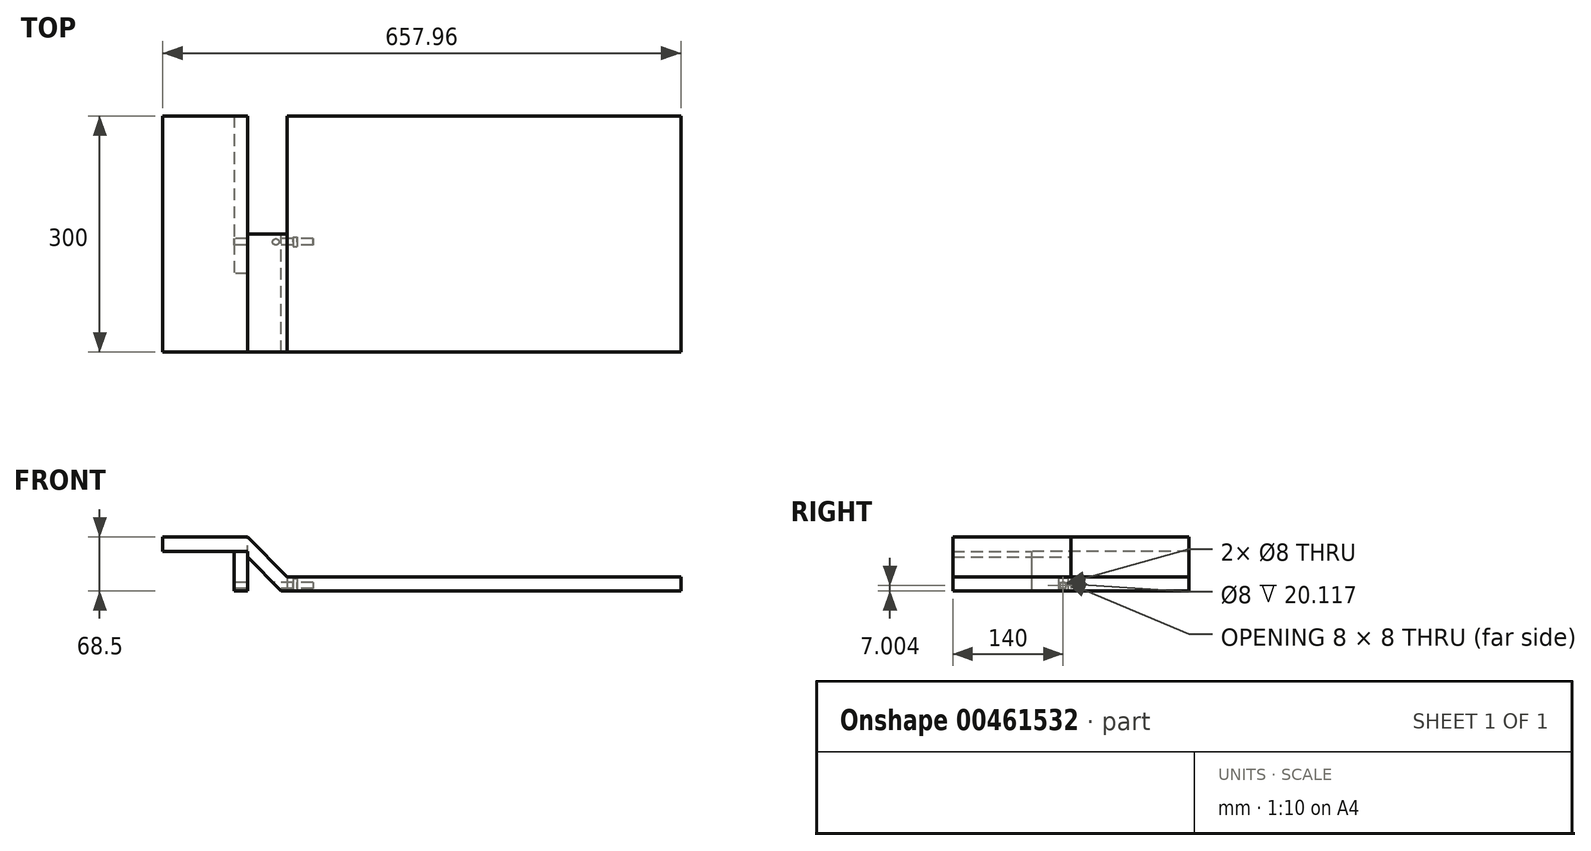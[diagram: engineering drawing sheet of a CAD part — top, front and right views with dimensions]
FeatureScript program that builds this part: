
annotation { "Feature Type Name" : "Feature", "Feature Type Description" : "" }
export const myFeature = defineFeature(function(context is Context, id is Id, definition is map)
    precondition{}
    {
        {
            var Q0;
            Q0=qCreatedBy(makeId("Front.planeOp"),FACE);
            var sketch = newSketch(context, id + "F0", { "sketchPlane" : qUnion([Q0])});
            skLineSegment(sketch, "E0.bottom", {"start": v(351.03, 31.5) * mm, "end": v(-148.97, 31.5) * mm});
            skLineSegment(sketch, "E0.top", {"start": v(351.03, 13.5) * mm, "end": v(-148.97, 13.5) * mm});
            skLineSegment(sketch, "E0.left", {"start": v(351.03, 31.5) * mm, "end": v(351.03, 13.5) * mm});
            skLineSegment(sketch, "E0.right", {"start": v(-148.97, 31.5) * mm, "end": v(-148.97, 13.5) * mm});
            skLineSegment(sketch, "E1.bottom", {"start": v(-148.97, 368.37) * mm, "end": v(-199.47, 368.37) * mm, "construction": true});
            skLineSegment(sketch, "E1.top", {"start": v(-148.97, -138.36) * mm, "end": v(-199.47, -138.36) * mm, "construction": true});
            skLineSegment(sketch, "E1.left", {"start": v(-148.97, 368.37) * mm, "end": v(-148.97, -138.36) * mm, "construction": true});
            skLineSegment(sketch, "E1.right", {"start": v(-199.47, 368.37) * mm, "end": v(-199.47, -138.36) * mm, "construction": true});
            skLineSegment(sketch, "E2", {"start": v(-148.97, 31.5) * mm, "end": v(-199.47, 82) * mm});
            skLineSegment(sketch, "E3", {"start": v(-148.97, 13.5) * mm, "end": v(-156.43, 13.5) * mm});
            skLineSegment(sketch, "E4", {"start": v(-156.43, 13.5) * mm, "end": v(-199.47, 56.54) * mm});
            skLineSegment(sketch, "E5", {"start": v(-199.47, 82) * mm, "end": v(-306.93, 82) * mm});
            skLineSegment(sketch, "E6", {"start": v(-199.47, 56.54) * mm, "end": v(-206.93, 64) * mm});
            skLineSegment(sketch, "E7", {"start": v(-206.93, 64) * mm, "end": v(-306.93, 64) * mm});
            skLineSegment(sketch, "E8", {"start": v(-306.93, 64) * mm, "end": v(-306.93, 82) * mm});
            skLineSegment(sketch, "E9", {"start": v(-199.47, 56.54) * mm, "end": v(-199.47, 82) * mm});
            skLineSegment(sketch, "E10.bottom", {"start": v(-216.3, 64) * mm, "end": v(-199.47, 64) * mm});
            skLineSegment(sketch, "E10.top", {"start": v(-216.3, 13.5) * mm, "end": v(-199.47, 13.5) * mm});
            skLineSegment(sketch, "E10.left", {"start": v(-216.3, 64) * mm, "end": v(-216.3, 13.5) * mm});
            skLineSegment(sketch, "E10.right", {"start": v(-199.47, 64) * mm, "end": v(-199.47, 13.5) * mm});
            skSolve(sketch);
        }
        {
            var Q0;
            Q0=makeQuery(id+"F0.imprint","IMPRINT",FACE,{"disambiguationData":[TD([[makeQuery(id+"F0.imprint","IMPRINT",EDGE,{"derivedFrom":sQuery(id+"F0.wireOp",EDGE,"E0.bottom")}),1.0]])]});
            extrude(context, id + "F1", {"entities" : qUnion([Q0]), "oppositeDirection" : true, "depth" : 150 * mm, "hasSecondDirection" : true, "secondDirectionOppositeDirection" : false, "secondDirectionDepth" : 150 * mm});
        }
        {
            var Q0;
            Q0=makeQuery(id+"F0.imprint","IMPRINT",FACE,{"disambiguationData":[TD([[makeQuery(id+"F0.imprint","IMPRINT",EDGE,{"derivedFrom":sQuery(id+"F0.wireOp",EDGE,"E0.right")}),-1.0]])]});
            extrude(context, id + "F2", {"entities" : qUnion([Q0]), "operationType" : NewBodyOperationType.ADD, "depth" : 150 * mm});
        }
        {
            var Q0;
            Q0=makeQuery(id+"F0.imprint","IMPRINT",FACE,{"disambiguationData":[TD([[makeQuery(id+"F0.imprint","IMPRINT",EDGE,{"derivedFrom":sQuery(id+"F0.wireOp",EDGE,"E5")}),1.0]])]});
            extrude(context, id + "F3", {"entities" : qUnion([Q0]), "operationType" : NewBodyOperationType.ADD, "depth" : 150 * mm, "hasSecondDirection" : true, "secondDirectionOppositeDirection" : true, "secondDirectionDepth" : 150 * mm});
        }
        {
            var Q0;
            {var subQ3=sQuery(id+"F0.wireOp",EDGE,"E6");Q0=makeQuery(id+"F0.imprint","IMPRINT",FACE,{"disambiguationData":[TD([[makeQuery(id+"F0.imprint","IMPRINT",EDGE,{"derivedFrom":subQ3}),1.0]])]});}
            var Q1;
            {var subQ0=sQuery(id+"F0.wireOp",EDGE,"E6");Q1=makeQuery(id+"F0.imprint","IMPRINT",FACE,{"disambiguationData":[TD([[makeQuery(id+"F0.imprint","IMPRINT",EDGE,{"derivedFrom":subQ0}),-1.0]])]});}
            extrude(context, id + "F4", {"entities" : qUnion([Q0, Q1]), "operationType" : NewBodyOperationType.ADD, "oppositeDirection" : true, "depth" : 150 * mm, "hasSecondDirection" : true, "secondDirectionOppositeDirection" : false, "secondDirectionDepth" : 50 * mm});
        }
        {
            var Q0;
            Q0=makeQuery(id+"F4.opExtrude","SWEPT_FACE",FACE,{"disambiguationData":[OSD([sQuery(id+"F0.wireOp",EDGE,"E10.left")])]});
            var sketch = newSketch(context, id + "F5", { "sketchPlane" : qUnion([Q0])});
            skCircle(sketch, "E11", {"center": v(10, 20.5) * mm, "radius": 4 * mm});
            skSolve(sketch);
        }
        {
            var Q0;
            Q0=makeQuery(id+"F5.imprint","IMPRINT",FACE,{"disambiguationData":[TD([[makeQuery(id+"F5.imprint","IMPRINT",EDGE,{"derivedFrom":sQuery(id+"F5.wireOp",EDGE,"E11")}),1.0]])]});
            extrude(context, id + "F6", {"entities" : qUnion([Q0]), "operationType" : NewBodyOperationType.REMOVE, "oppositeDirection" : true, "depth" : 100 * mm});
        }
        {
            var Q0;
            Q0=makeQuery(id+"F2.boolean.opBoolean","MERGE",FACE,{"derivedFrom":[makeQuery(id+"F1.opExtrude","SWEPT_FACE",FACE,{"disambiguationData":[OSD([sQuery(id+"F0.wireOp",EDGE,"E0.top")])]}),makeQuery(id+"F2.opExtrude","SWEPT_FACE",FACE,{"disambiguationData":[OSD([sQuery(id+"F0.wireOp",EDGE,"E3")])]})]});
            var sketch = newSketch(context, id + "F7", { "sketchPlane" : qUnion([Q0])});
            skLineSegment(sketch, "E12.bottom", {"start": v(-141.43, 4) * mm, "end": v(-136.43, 4) * mm});
            skLineSegment(sketch, "E12.top", {"start": v(-141.43, 16) * mm, "end": v(-136.43, 16) * mm});
            skLineSegment(sketch, "E12.left", {"start": v(-141.43, 4) * mm, "end": v(-141.43, 16) * mm});
            skLineSegment(sketch, "E12.right", {"start": v(-136.43, 4) * mm, "end": v(-136.43, 16) * mm});
            skSolve(sketch);
        }
        {
            var Q0;
            Q0 = qSketchRegion(id + "F7", true);
            extrude(context, id + "F8", {"entities" : qUnion([Q0]), "operationType" : NewBodyOperationType.REMOVE, "oppositeDirection" : true, "depth" : 16 * mm});
        }
    });
